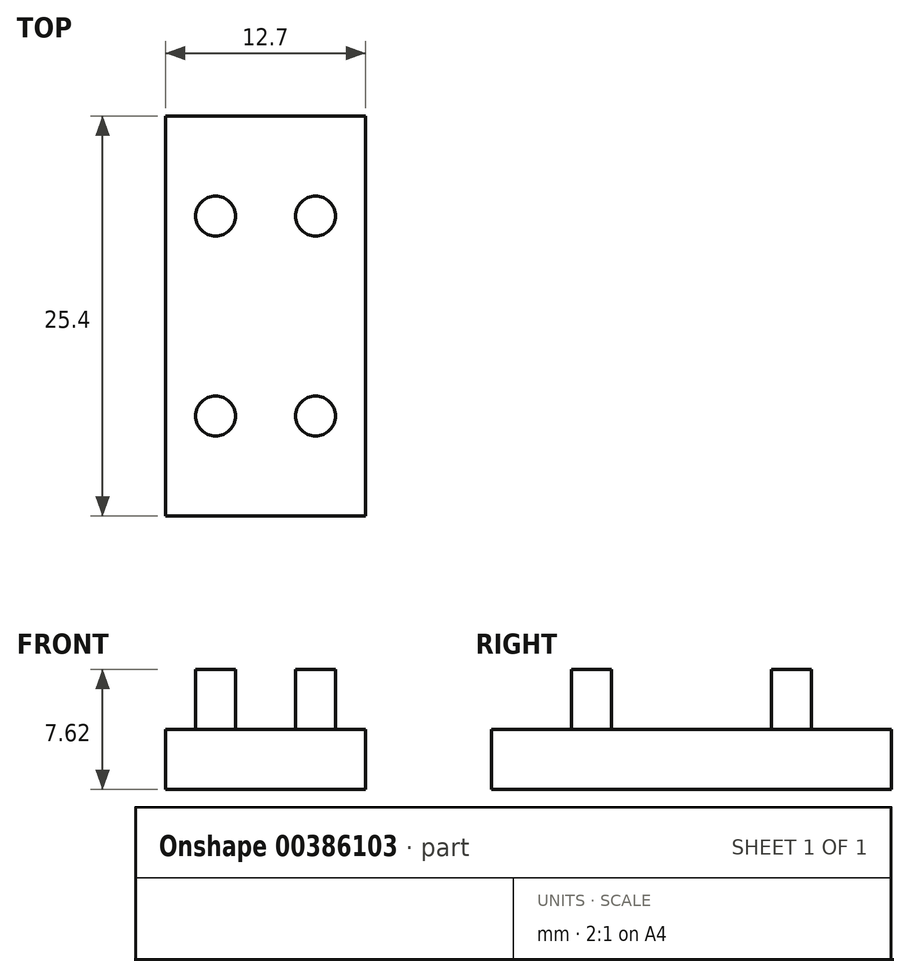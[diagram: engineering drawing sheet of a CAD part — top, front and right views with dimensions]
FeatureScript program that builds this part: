
annotation { "Feature Type Name" : "Feature", "Feature Type Description" : "" }
export const myFeature = defineFeature(function(context is Context, id is Id, definition is map)
    precondition{}
    {
        {
            var Q0;
            Q0=qCreatedBy(makeId("Top.planeOp"),FACE);
            var sketch = newSketch(context, id + "F0", { "sketchPlane" : qUnion([Q0])});
            skLineSegment(sketch, "E0.bottom", {"start": v(6.35, 12.7) * mm, "end": v(-6.35, 12.7) * mm});
            skLineSegment(sketch, "E0.top", {"start": v(6.35, -12.7) * mm, "end": v(-6.35, -12.7) * mm});
            skLineSegment(sketch, "E0.left", {"start": v(6.35, 12.7) * mm, "end": v(6.35, -12.7) * mm});
            skLineSegment(sketch, "E0.right", {"start": v(-6.35, 12.7) * mm, "end": v(-6.35, -12.7) * mm});
            skPoint(sketch, "E0.middle", {"position": v(0, 0) * mm});
            skSolve(sketch);
        }
        {
            var Q0;
            Q0 = qSketchRegion(id + "F0", true);
            extrude(context, id + "F1", {"entities" : qUnion([Q0]), "depth" : 3.8 * mm});
        }
        {
            var Q0;
            Q0=makeQuery(id+"F1.opExtrude","CAP_FACE",FACE,{"disambiguationData":[OSD([sQuery(id+"F0.wireOp",EDGE,"E0.bottom"),sQuery(id+"F0.wireOp",EDGE,"E0.top"),sQuery(id+"F0.wireOp",EDGE,"E0.left"),sQuery(id+"F0.wireOp",EDGE,"E0.right")])],"isStart":false});
            var sketch = newSketch(context, id + "F2", { "sketchPlane" : qUnion([Q0])});
            skCircle(sketch, "E1", {"center": v(-3.18, 6.35) * mm, "radius": 1.27 * mm});
            skCircle(sketch, "E2.MirrorC", {"center": v(3.18, 6.35) * mm, "radius": 1.27 * mm});
            skCircle(sketch, "E3.MirrorC", {"center": v(3.18, -6.35) * mm, "radius": 1.27 * mm});
            skCircle(sketch, "E4.MirrorC", {"center": v(-3.18, -6.35) * mm, "radius": 1.27 * mm});
            skSolve(sketch);
        }
        {
            var Q0;
            Q0 = qSketchRegion(id + "F2", true);
            extrude(context, id + "F3", {"entities" : qUnion([Q0]), "operationType" : NewBodyOperationType.ADD, "depth" : 3.8 * mm});
        }
    });
